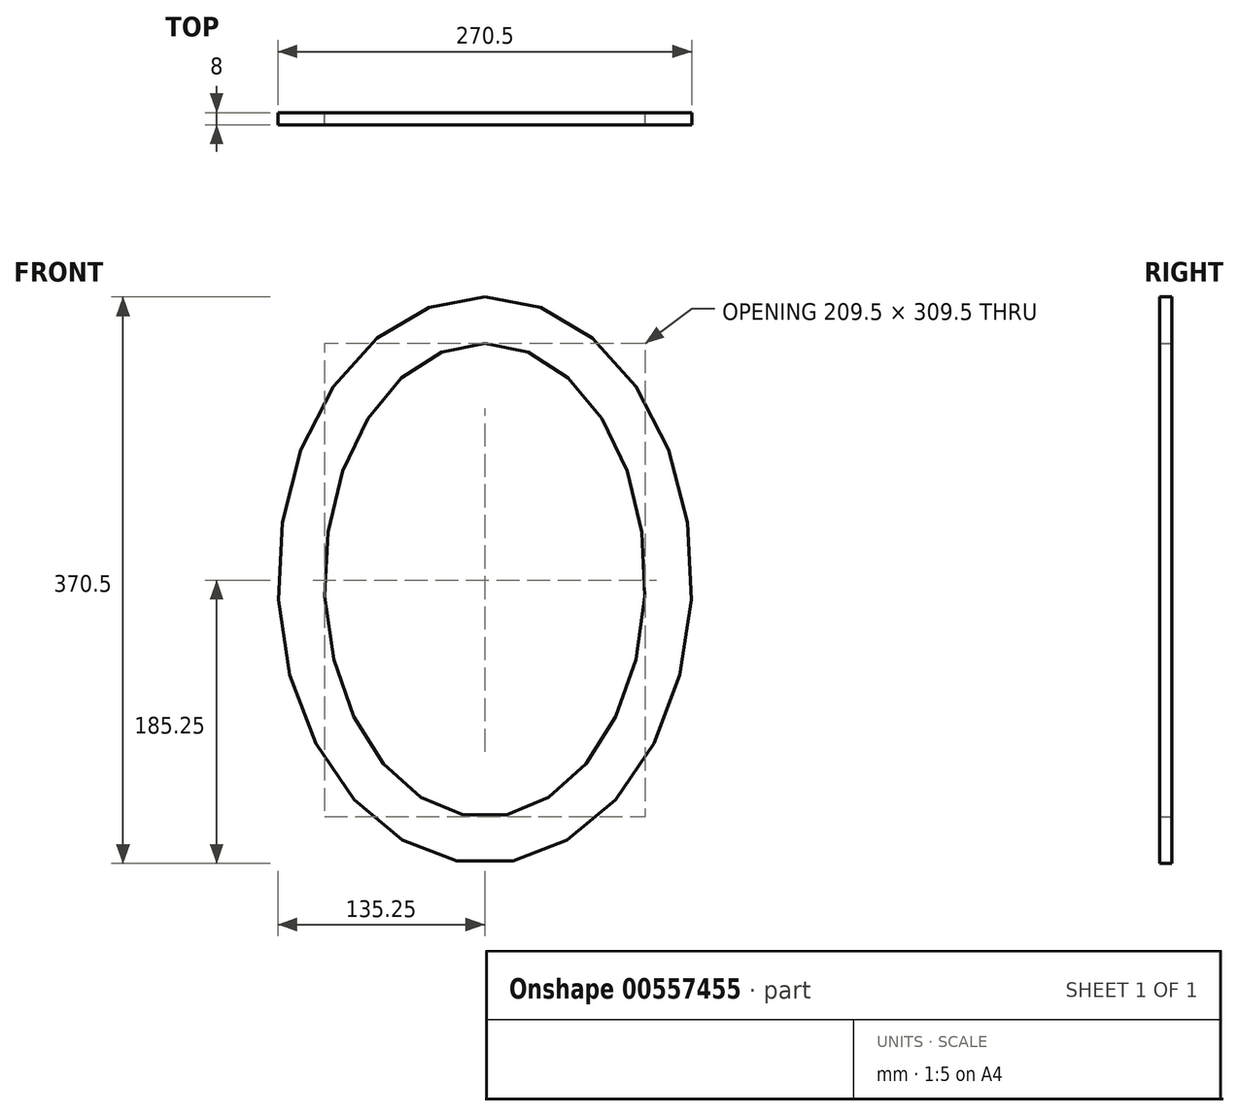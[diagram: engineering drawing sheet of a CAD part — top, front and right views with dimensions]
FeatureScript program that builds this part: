
annotation { "Feature Type Name" : "Feature", "Feature Type Description" : "" }
export const myFeature = defineFeature(function(context is Context, id is Id, definition is map)
    precondition{}
    {
        {
            var Q0;
            Q0=qCreatedBy(makeId("Front.planeOp"),FACE);
            var sketch = newSketch(context, id + "F0", { "sketchPlane" : qUnion([Q0])});
            skCircle(sketch, "E0", {"center": v(119.75, 0) * mm, "radius": 10 * mm, "construction": true});
            skCircle(sketch, "E1", {"center": v(119.75, 0) * mm, "radius": 15 * mm, "construction": true});
            skEllipse(sketch, "E2", {"center": v(0, 0) * mm, "majorRadius": 109.75 * mm, "minorRadius": 159.75 * mm, "majorAxis": v(1, 0), "construction": true});
            skEllipse(sketch, "E3", {"center": v(0, 0) * mm, "majorRadius": 104.75 * mm, "minorRadius": 154.75 * mm, "majorAxis": v(1, 0)});
            skLineSegment(sketch, "E4", {"start": v(0, 159.75) * mm, "end": v(0, 154.75) * mm, "construction": true});
            skLineSegment(sketch, "E5", {"start": v(-109.75, 0) * mm, "end": v(-104.75, 0) * mm, "construction": true});
            skEllipse(sketch, "E6", {"center": v(0, 0) * mm, "majorRadius": 135.25 * mm, "minorRadius": 185.25 * mm, "majorAxis": v(1, 0)});
            skLineSegment(sketch, "E7", {"start": v(0, 154.75) * mm, "end": v(0, 185.25) * mm, "construction": true});
            skLineSegment(sketch, "E8", {"start": v(-104.75, 0) * mm, "end": v(-135.25, 0) * mm, "construction": true});
            skSolve(sketch);
        }
        {
            var Q0;
            Q0 = qSketchRegion(id + "F0", true);
            extrude(context, id + "F1", {"entities" : qUnion([Q0]), "depth" : 8 * mm, "offsetDistance" : 25 * mm});
        }
    });
